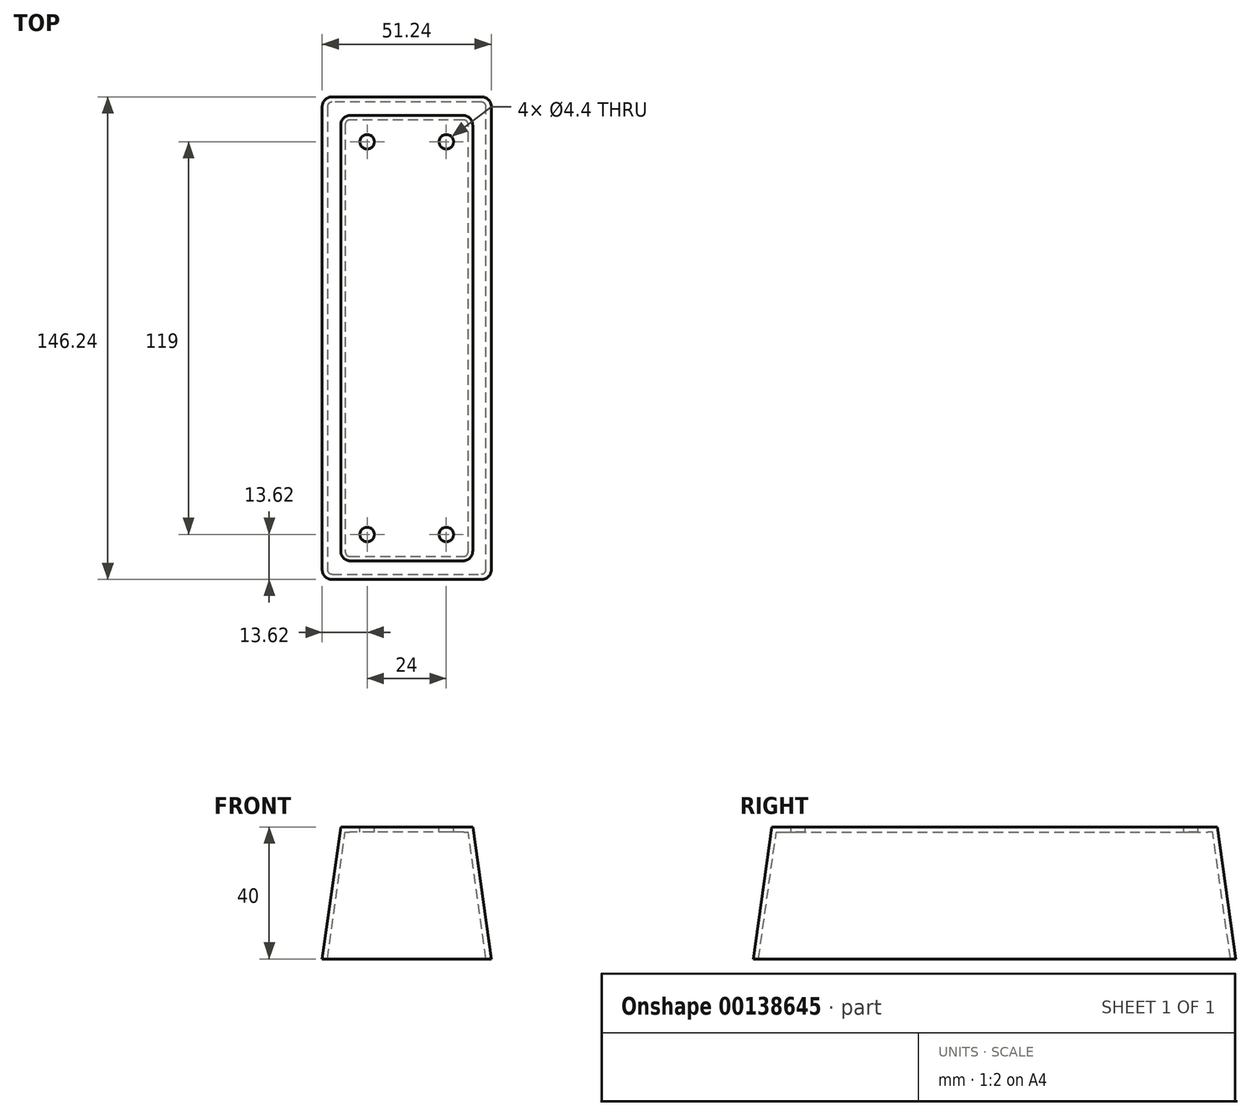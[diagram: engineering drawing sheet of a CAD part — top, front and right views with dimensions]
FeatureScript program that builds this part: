
annotation { "Feature Type Name" : "Feature", "Feature Type Description" : "" }
export const myFeature = defineFeature(function(context is Context, id is Id, definition is map)
    precondition{}
    {
        {
            var Q0;
            Q0=qCreatedBy(makeId("Top.planeOp"),FACE);
            var sketch = newSketch(context, id + "F0", { "sketchPlane" : qUnion([Q0])});
            skLineSegment(sketch, "E0.bottom", {"start": v(20, 67.5) * mm, "end": v(-20, 67.5) * mm});
            skLineSegment(sketch, "E0.top", {"start": v(20, -67.5) * mm, "end": v(-20, -67.5) * mm});
            skLineSegment(sketch, "E0.left", {"start": v(20, 67.5) * mm, "end": v(20, -67.5) * mm});
            skLineSegment(sketch, "E0.right", {"start": v(-20, 67.5) * mm, "end": v(-20, -67.5) * mm});
            skPoint(sketch, "E0.middle", {"position": v(0, 0) * mm});
            skSolve(sketch);
        }
        {
            var Q0;
            Q0=makeQuery(id+"F0.imprint","IMPRINT",FACE,{"disambiguationData":[TD([[makeQuery(id+"F0.imprint","IMPRINT",EDGE,{"derivedFrom":sQuery(id+"F0.wireOp",EDGE,"E0.bottom")}),1.0]])]});
            extrude(context, id + "F1", {"entities" : qUnion([Q0]), "oppositeDirection" : true, "depth" : 40 * mm, "hasDraft" : true, "draftAngle" : 8 * degree});
        }
        {
            var Q0;
            Q0=makeQuery(id+"F1.opExtrude","SWEPT_EDGE",EDGE,{"disambiguationData":[OSD([sQuery(id+"F0.wireOp",EDGE,"E0.top"),sQuery(id+"F0.wireOp",EDGE,"E0.right")])]});
            var Q1;
            Q1=makeQuery(id+"F1.opExtrude","SWEPT_EDGE",EDGE,{"disambiguationData":[OSD([sQuery(id+"F0.wireOp",EDGE,"E0.bottom"),sQuery(id+"F0.wireOp",EDGE,"E0.right")])]});
            var Q2;
            Q2=makeQuery(id+"F1.opExtrude","SWEPT_EDGE",EDGE,{"disambiguationData":[OSD([sQuery(id+"F0.wireOp",EDGE,"E0.top"),sQuery(id+"F0.wireOp",EDGE,"E0.left")])]});
            var Q3;
            Q3=makeQuery(id+"F1.opExtrude","SWEPT_EDGE",EDGE,{"disambiguationData":[OSD([sQuery(id+"F0.wireOp",EDGE,"E0.bottom"),sQuery(id+"F0.wireOp",EDGE,"E0.left")])]});
            fillet(context, id + "F2", {"entities" : qUnion([Q0, Q1, Q2, Q3]), "radius" : 3 * mm, "tangentPropagation" : true, "allowEdgeOverflow" : false});
        }
        {
            var Q0;
            Q0=makeQuery(id+"F1.opExtrude","CAP_FACE",FACE,{"disambiguationData":[OSD([sQuery(id+"F0.wireOp",EDGE,"E0.bottom"),sQuery(id+"F0.wireOp",EDGE,"E0.top"),sQuery(id+"F0.wireOp",EDGE,"E0.left"),sQuery(id+"F0.wireOp",EDGE,"E0.right")])],"isStart":false});
            shell(context, id + "F3", {"entities" : qUnion([Q0]), "thickness" : 1.58 * mm});
        }
        {
            var Q0;
            Q0=makeQuery(id+"F1.opExtrude","CAP_FACE",FACE,{"disambiguationData":[OSD([sQuery(id+"F0.wireOp",EDGE,"E0.bottom"),sQuery(id+"F0.wireOp",EDGE,"E0.top"),sQuery(id+"F0.wireOp",EDGE,"E0.left"),sQuery(id+"F0.wireOp",EDGE,"E0.right")])],"isStart":true});
            var sketch = newSketch(context, id + "F4", { "sketchPlane" : qUnion([Q0])});
            skPoint(sketch, "E1", {"position": v(-12, 59.5) * mm});
            skPoint(sketch, "E2", {"position": v(12, 59.5) * mm});
            skPoint(sketch, "E3", {"position": v(-12, -59.5) * mm});
            skPoint(sketch, "E4", {"position": v(12, -59.5) * mm});
            skSolve(sketch);
        }
        {
            var Q0;
            Q0=sQuery(id+"F4.wireOp",VERTEX,"E1");
            var Q1;
            Q1=sQuery(id+"F4.wireOp",VERTEX,"E3");
            var Q2;
            Q2=sQuery(id+"F4.wireOp",VERTEX,"E4");
            var Q3;
            Q3=sQuery(id+"F4.wireOp",VERTEX,"E2");
            var Q4;
            Q4=makeQuery(id+"F1.opExtrude","SWEPT_BODY",BODY,{"disambiguationData":[OSD([sQuery(id+"F0.wireOp",EDGE,"E0.bottom"),sQuery(id+"F0.wireOp",EDGE,"E0.top"),sQuery(id+"F0.wireOp",EDGE,"E0.left"),sQuery(id+"F0.wireOp",EDGE,"E0.right")])]});
            hole(context, id + "F5", {"style" : HoleStyle.SIMPLE, "endStyle" : HoleEndStyle.THROUGH, "standardTappedOrClearance" : lookupTablePath({ "standard" : "ISO", "fit" : "Normal", "size" : "M4", "type" : "Clearance" }), "standardBlindInLast" : lookupTablePath({ "fit" : "Standard", "standard" : "ISO", "size" : "M4", "type" : "Clearance" }), "holeDiameter" : 4.4 * mm, "locations" : qUnion([Q0, Q1, Q2, Q3]), "scope" : qUnion([Q4]), "isTappedThrough" : true});
        }
    });
